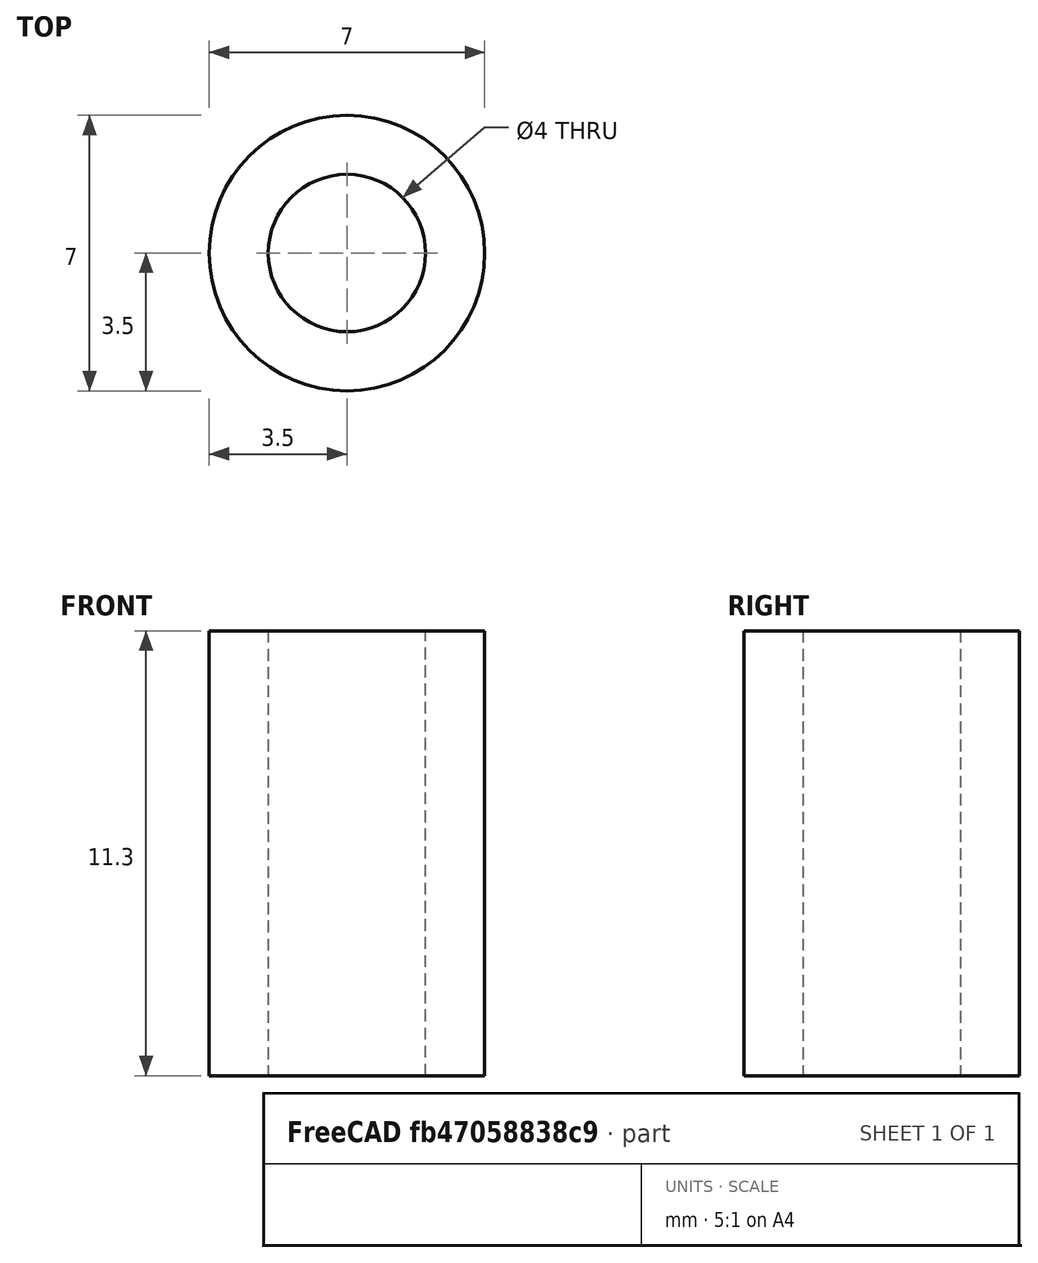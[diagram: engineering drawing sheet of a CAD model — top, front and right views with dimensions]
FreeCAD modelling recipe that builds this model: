
FCSTD DOCUMENT  (FreeCAD 0.19R24291 (Git))
Label: SpacerStepper
License: All rights reserved
LicenseURL: http://en.wikipedia.org/wiki/All_rights_reserved
objects: PartDesign::CoordinateSystem×1, Sketcher::SketchObject×1, PartDesign::Pad×1, PartDesign::Body×1, App::Part×1
note: 5 computed .brp shape members not serialized (recipe doc carries the construction recipe); baked Part::Feature solids carry a one-line shape summary decoded from their .brp
EXTERNAL_REF file=data.FCStd obj=Spreadsheet

FEATURE [PartDesign::CoordinateSystem] LCS_0
  AttacherType = Attacher::AttachEngine3D
  MapMode = 2
  Support = -> [X_Axis]
FEATURE [Sketcher::SketchObject] Sketch
  FullyConstrained = true
  MapMode = 5
  Support = -> [XY_Plane001]
  expr: Constraints[3] = data#<<data>>.StepperMountOutsideDiameter
  expr: Constraints[2] = data#<<data>>.StepperMountSpacerHole
  sketch-geometry (2):
    g0: Circle CenterX=0 CenterY=0 CenterZ=0 NormalX=0 NormalY=0 NormalZ=1 AngleXU=0 Radius=2
    g1: Circle CenterX=0 CenterY=0 CenterZ=0 NormalX=0 NormalY=0 NormalZ=1 AngleXU=0 Radius=3.5
  constraints (4):
    c: Coincident(g0,g-1)
    c: Coincident(g1,g0)
    c: Diameter(g0) = 4
    c: Diameter(g1) = 7
FEATURE [PartDesign::Pad] Pad
  Direction = (1,1,1)
  Length = 11.3
  Length2 = 100
  Profile = -> Sketch
  Type = 0
  expr: Length = data#<<data>>.PCBStepperSpacerLength
FEATURE [PartDesign::Body] Body
  Group = -> [Sketch,Pad]
  Origin = -> Origin001
  Tip = -> Pad
FEATURE [App::Part] Part_spacer_stepper
  Group = -> [LCS_0,Body]
  Origin = -> Origin
